FCSTD DOCUMENT  (FreeCAD 0.19R)
Label: Formato_da_placa
License: All rights reserved
LicenseURL: http://en.wikipedia.org/wiki/All_rights_reserved
objects: Sketcher::SketchObject×1
note: 1 computed .brp shape members not serialized (recipe doc carries the construction recipe); baked Part::Feature solids carry a one-line shape summary decoded from their .brp

FEATURE [Sketcher::SketchObject] Sketch
  FullyConstrained = false
  sketch-geometry (18):
    g0: LineSegment StartX=-46.5 StartY=35 StartZ=0 EndX=46.5 EndY=35 EndZ=0
    g1: LineSegment StartX=46.5 StartY=35 StartZ=0 EndX=46.5 EndY=-35 EndZ=0
    g2: LineSegment StartX=46.5 StartY=-35 StartZ=0 EndX=-46.5 EndY=-35 EndZ=0
    g3: LineSegment StartX=-46.5 StartY=-35 StartZ=0 EndX=-46.5 EndY=35 EndZ=0
    g4: Circle CenterX=-44.15 CenterY=32.65 CenterZ=0 NormalX=0 NormalY=0 NormalZ=1 AngleXU=0 Radius=1.25
    g5: Circle CenterX=44.15 CenterY=32.65 CenterZ=0 NormalX=0 NormalY=0 NormalZ=1 AngleXU=0 Radius=1.25
    g6: Circle CenterX=44.15 CenterY=-32.65 CenterZ=0 NormalX=0 NormalY=0 NormalZ=1 AngleXU=0 Radius=1.25
    g7: Circle CenterX=-44.15 CenterY=-32.65 CenterZ=0 NormalX=0 NormalY=0 NormalZ=1 AngleXU=0 Radius=1.25
    g8: LineSegment StartX=-44.15 StartY=32.65 StartZ=0 EndX=-46.5 EndY=32.65 EndZ=0
    g9: LineSegment StartX=-44.15 StartY=32.65 StartZ=0 EndX=-44.15 EndY=35 EndZ=0
    g10: LineSegment StartX=44.15 StartY=32.65 StartZ=0 EndX=44.15 EndY=35 EndZ=0
    g11: LineSegment StartX=44.15 StartY=32.65 StartZ=0 EndX=46.5 EndY=32.65 EndZ=0
    g12: LineSegment StartX=-44.15 StartY=-32.65 StartZ=0 EndX=-46.5 EndY=-32.65 EndZ=0
    g13: LineSegment StartX=-44.15 StartY=-32.65 StartZ=0 EndX=-44.15 EndY=-35 EndZ=0
    g14: LineSegment StartX=44.15 StartY=-32.65 StartZ=0 EndX=46.5 EndY=-32.65 EndZ=0
    g15: LineSegment StartX=44.15 StartY=-32.65 StartZ=0 EndX=44.15 EndY=-35 EndZ=0
    g16: LineSegment StartX=-46.5 StartY=35 StartZ=0 EndX=46.5 EndY=-35 EndZ=0
    g17: GeomPoint X=0 Y=0 Z=0
  constraints (49):
    c: Coincident(g0,g1)
    c: Coincident(g1,g2)
    c: Coincident(g2,g3)
    c: Coincident(g3,g0)
    c: Horizontal(g0)
    c: Horizontal(g2)
    c: Vertical(g1)
    c: Vertical(g3)
    c: Distance(g0) = 93
    c: Distance(g1) = 70
    c: Diameter(g4) = 2.5
    c: Equal(g4,g5) = 2.5
    c: Equal(g4,g7) = 2.5
    c: Coincident(g8,g4)
    c: PointOnObject(g8,g3)
    c: Horizontal(g8)
    c: Coincident(g9,g4)
    c: PointOnObject(g9,g0)
    c: Vertical(g9)
    c: Distance(g8) = 2.35
    c: Distance(g9) = 2.35
    c: Coincident(g10,g5)
    c: PointOnObject(g10,g0)
    c: Coincident(g11,g5)
    c: PointOnObject(g11,g1)
    c: Horizontal(g11)
    c: Vertical(g10)
    c: Distance(g11) = 2.35
    c: Distance(g10) = 2.35
    c: Coincident(g12,g7)
    c: PointOnObject(g12,g3)
    c: Horizontal(g12)
    c: Coincident(g13,g7)
    c: PointOnObject(g13,g2)
    c: Vertical(g13)
    c: Distance(g12) = 2.35
    c: Distance(g13) = 2.35
    c: Coincident(g14,g6)
    c: PointOnObject(g14,g1)
    c: Horizontal(g14)
    c: Coincident(g15,g6)
    c: PointOnObject(g15,g2)
    c: Vertical(g15)
    c: Distance(g14) = 2.35
    c: Distance(g15) = 2.35
    c: Coincident(g16,g0)
    c: Coincident(g16,g1)
    c: Symmetric(g0,g1,g17)
    c: Coincident(g17,g-1)
